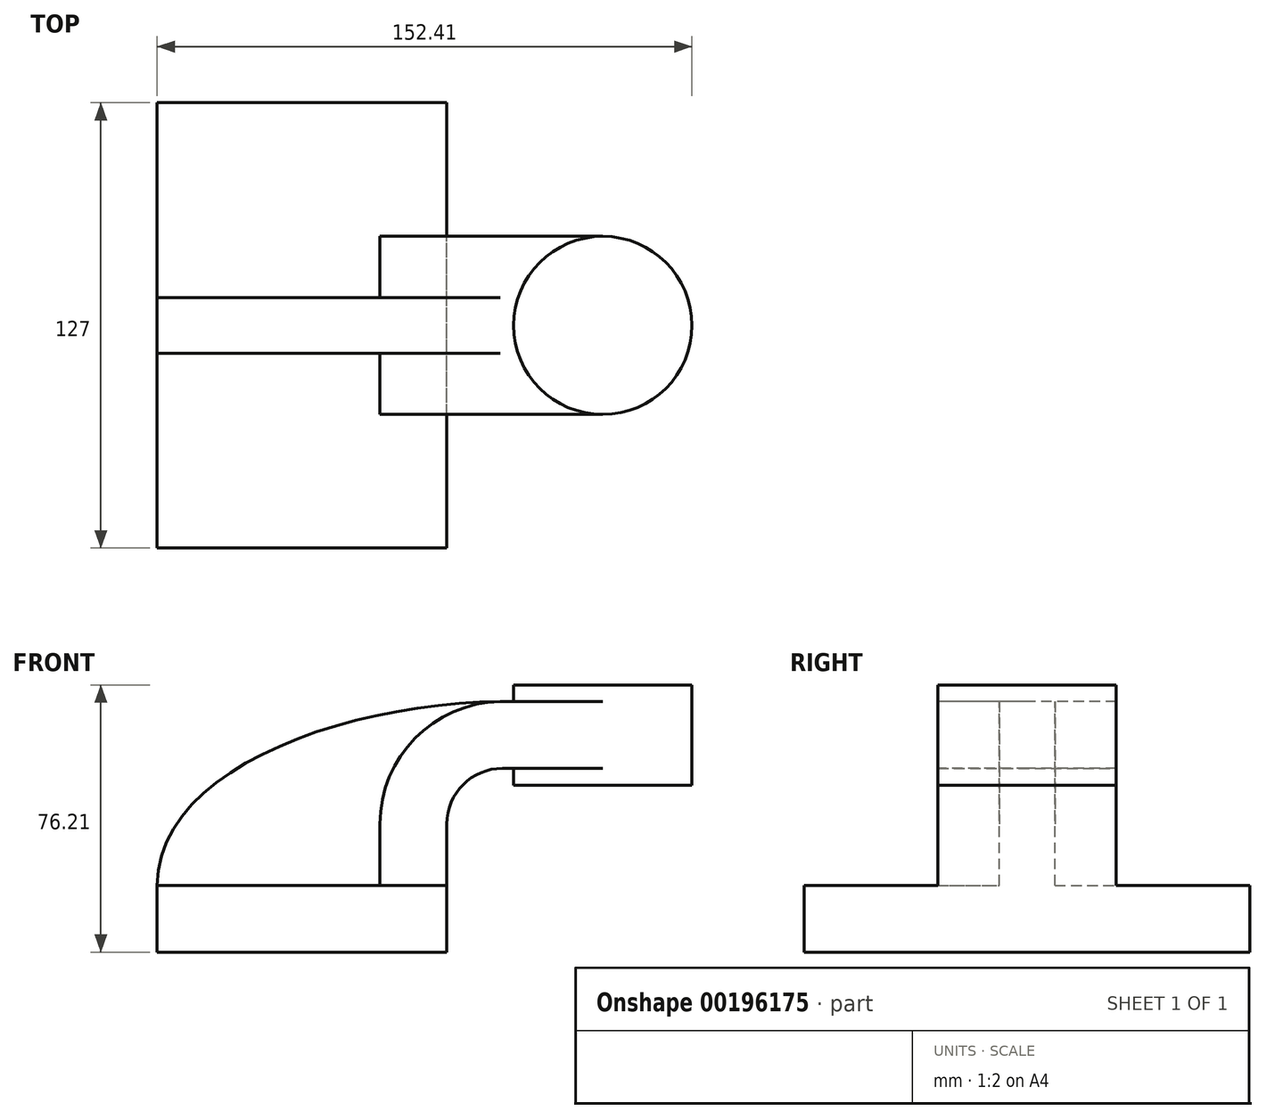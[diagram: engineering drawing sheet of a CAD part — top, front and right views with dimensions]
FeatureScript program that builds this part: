
annotation { "Feature Type Name" : "Feature", "Feature Type Description" : "" }
export const myFeature = defineFeature(function(context is Context, id is Id, definition is map)
    precondition{}
    {
        {
            var Q0;
            Q0=qCreatedBy(makeId("Front.planeOp"),FACE);
            var sketch = newSketch(context, id + "F0", { "sketchPlane" : qUnion([Q0])});
            skLineSegment(sketch, "E0.bottom", {"start": v(41.27, 9.53) * mm, "end": v(-41.28, 9.53) * mm});
            skLineSegment(sketch, "E0.top", {"start": v(41.28, -9.52) * mm, "end": v(-41.27, -9.52) * mm});
            skLineSegment(sketch, "E0.left", {"start": v(41.27, 9.53) * mm, "end": v(41.28, -9.52) * mm});
            skLineSegment(sketch, "E0.right", {"start": v(-41.28, 9.53) * mm, "end": v(-41.27, -9.52) * mm});
            skPoint(sketch, "E0.middle", {"position": v(0, 0) * mm});
            skLineSegment(sketch, "E1.bottom", {"start": v(111.13, 38.1) * mm, "end": v(60.33, 38.1) * mm});
            skLineSegment(sketch, "E1.top", {"start": v(111.13, 66.68) * mm, "end": v(60.33, 66.68) * mm});
            skLineSegment(sketch, "E1.left", {"start": v(111.13, 38.1) * mm, "end": v(111.13, 66.68) * mm});
            skLineSegment(sketch, "E1.right", {"start": v(60.33, 38.1) * mm, "end": v(60.33, 66.68) * mm});
            skPoint(sketch, "E1.middle", {"position": v(85.73, 52.39) * mm});
            skLineSegment(sketch, "E2", {"start": v(41.27, 9.53) * mm, "end": v(41.27, 27) * mm});
            skArc(sketch, "E3", {"start": v(41.27, 27) * mm, "mid": v(45.92, 38.23) * mm, "end": v(57.15, 42.88) * mm});
            skLineSegment(sketch, "E4", {"start": v(57.15, 42.88) * mm, "end": v(85.73, 42.88) * mm});
            skLineSegment(sketch, "E5.0", {"start": v(57.15, 61.93) * mm, "end": v(85.73, 61.93) * mm});
            skArc(sketch, "E5.1", {"start": v(22.22, 27) * mm, "mid": v(32.45, 51.7) * mm, "end": v(57.15, 61.93) * mm});
            skLineSegment(sketch, "E5.2", {"start": v(22.22, 9.53) * mm, "end": v(22.22, 27) * mm});
            skLineSegment(sketch, "E6", {"start": v(85.73, 38.1) * mm, "end": v(85.73, 66.68) * mm});
            skFitSpline(sketch, "E7", {"points": [v(-41.28, 9.53) * mm, v(57.15, 61.93) * mm], "startDerivative": vector(0.8, 100.4) * mm, "endDerivative": vector(133.47, 0.97) * mm});
            skSolve(sketch);
        }
        {
            var Q0;
            Q0=makeQuery(id+"F0.imprint","IMPRINT",FACE,{"disambiguationData":[TD([[makeQuery(id+"F0.imprint","IMPRINT",EDGE,{"derivedFrom":sQuery(id+"F0.wireOp",EDGE,"E0.top")}),-1.0]])]});
            extrude(context, id + "F1", {"entities" : qUnion([Q0]), "endBound" : BoundingType.SYMMETRIC, "depth" : 127 * mm});
        }
        {
            var Q0;
            {var subQ0=sQuery(id+"F0.wireOp",EDGE,"E4");var subQ1=sQuery(id+"F0.wireOp",EDGE,"E1.right");var subQ2=makeQuery(id+"F0.imprint","INTERSECT",VERTEX,{"derivedFrom":[subQ1,subQ0]});Q0=makeQuery(id+"F0.imprint","IMPRINT",FACE,{"disambiguationData":[TD([[makeQuery(id+"F0.imprint","IMPRINT",EDGE,{"disambiguationData":[TD([[subQ2,-1.0]])],"derivedFrom":subQ1}),-1.0]])]});}
            var Q1;
            {var subQ1=sQuery(id+"F0.wireOp",EDGE,"E2");Q1=makeQuery(id+"F0.imprint","IMPRINT",FACE,{"disambiguationData":[TD([[makeQuery(id+"F0.imprint","IMPRINT",EDGE,{"derivedFrom":subQ1}),1.0]])]});}
            extrude(context, id + "F2", {"entities" : qUnion([Q0, Q1]), "operationType" : NewBodyOperationType.ADD, "endBound" : BoundingType.SYMMETRIC, "depth" : 50.8 * mm});
        }
        {
            var Q0;
            {var subQ3=sQuery(id+"F0.wireOp",EDGE,"E5.2");Q0=makeQuery(id+"F0.imprint","IMPRINT",FACE,{"disambiguationData":[TD([[makeQuery(id+"F0.imprint","IMPRINT",EDGE,{"derivedFrom":subQ3}),1.0]])]});}
            extrude(context, id + "F3", {"entities" : qUnion([Q0]), "operationType" : NewBodyOperationType.ADD, "endBound" : BoundingType.SYMMETRIC, "depth" : 15.88 * mm});
        }
        {
            var Q0;
            {var subQ0=sQuery(id+"F0.wireOp",EDGE,"E1.left");Q0=makeQuery(id+"F0.imprint","IMPRINT",FACE,{"disambiguationData":[TD([[makeQuery(id+"F0.imprint","IMPRINT",EDGE,{"derivedFrom":subQ0}),1.0]])]});}
            var Q1;
            Q1=sQuery(id+"F0.wireOp",EDGE,"E6");
            revolve(context, id + "F4", {"operationType" : NewBodyOperationType.ADD, "entities" : qUnion([Q0]), "axis" : qUnion([Q1]), "revolveType" : RevolveType.FULL});
        }
    });
